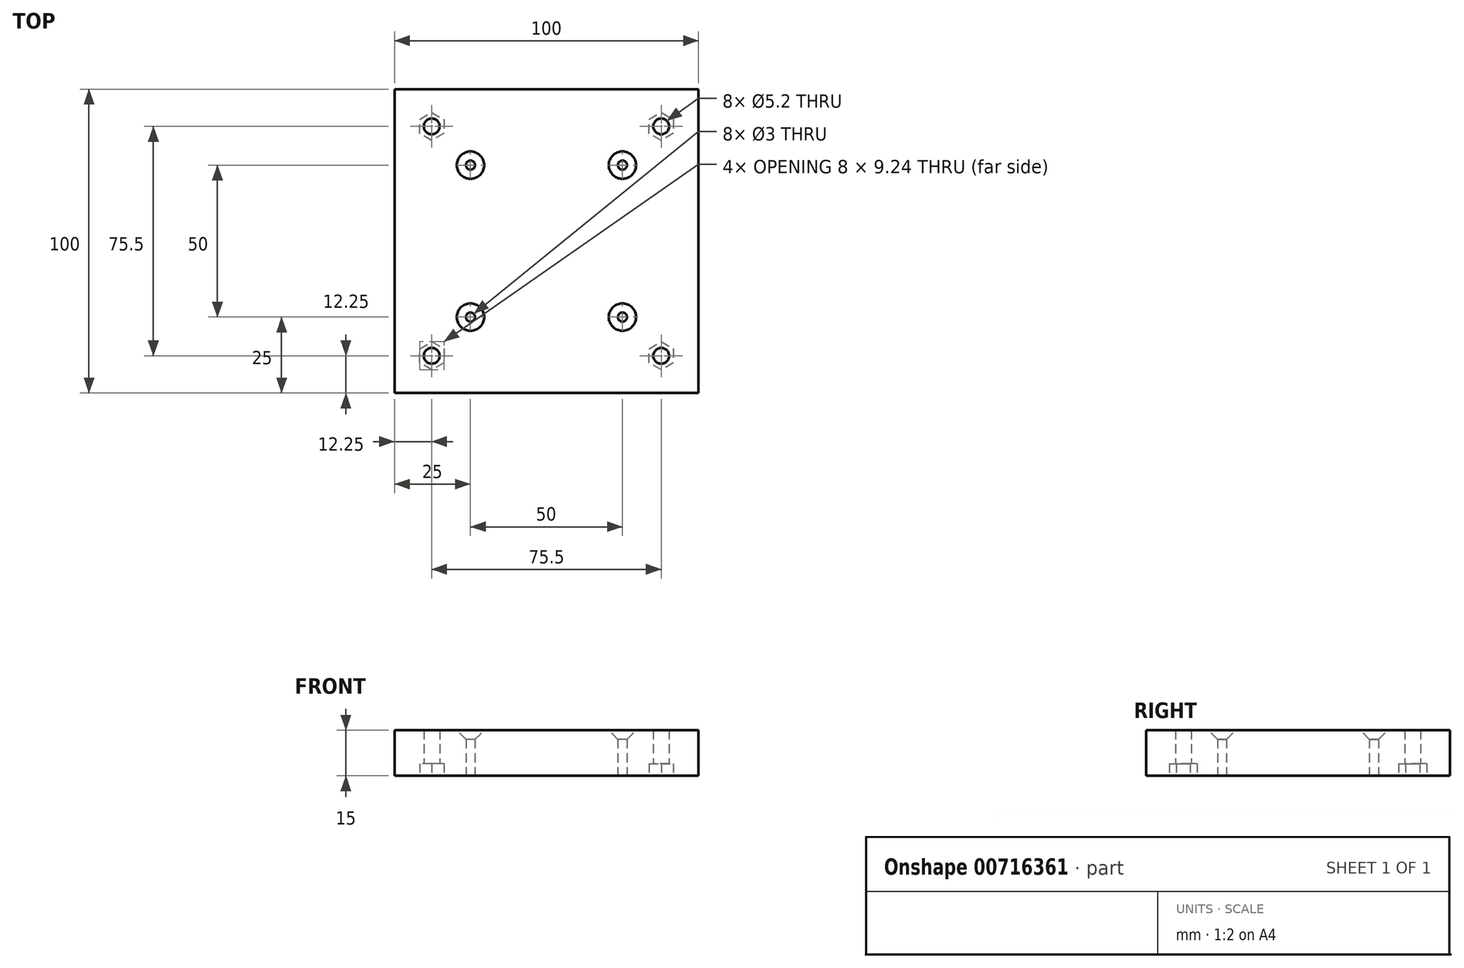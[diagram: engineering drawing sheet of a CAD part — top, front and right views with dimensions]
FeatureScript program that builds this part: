
annotation { "Feature Type Name" : "Feature", "Feature Type Description" : "" }
export const myFeature = defineFeature(function(context is Context, id is Id, definition is map)
    precondition{}
    {
        {
            var Q0;
            Q0=qCreatedBy(makeId("Top.planeOp"),FACE);
            var sketch = newSketch(context, id + "F0", { "sketchPlane" : qUnion([Q0])});
            skLineSegment(sketch, "E0.bottom", {"start": v(-50, 50) * mm, "end": v(50, 50) * mm});
            skLineSegment(sketch, "E0.top", {"start": v(-50, -50) * mm, "end": v(50, -50) * mm});
            skLineSegment(sketch, "E0.left", {"start": v(-50, 50) * mm, "end": v(-50, -50) * mm});
            skLineSegment(sketch, "E0.right", {"start": v(50, 50) * mm, "end": v(50, -50) * mm});
            skCircle(sketch, "E1", {"center": v(-37.75, 37.75) * mm, "radius": 2.6 * mm});
            skCircle(sketch, "E2", {"center": v(-37.75, -37.75) * mm, "radius": 2.6 * mm});
            skCircle(sketch, "E3", {"center": v(37.75, 37.75) * mm, "radius": 2.6 * mm});
            skCircle(sketch, "E4", {"center": v(37.75, -37.75) * mm, "radius": 2.6 * mm});
            skCircle(sketch, "E5.cCircle", {"center": v(-37.75, 37.75) * mm, "radius": 4 * mm, "construction": true});
            skLineSegment(sketch, "E5.0", {"start": v(-41.75, 35.44) * mm, "end": v(-41.75, 40.06) * mm});
            skLineSegment(sketch, "E5.1", {"start": v(-41.75, 40.06) * mm, "end": v(-37.75, 42.37) * mm});
            skLineSegment(sketch, "E5.2", {"start": v(-37.75, 42.37) * mm, "end": v(-33.75, 40.06) * mm});
            skLineSegment(sketch, "E5.3", {"start": v(-33.75, 40.06) * mm, "end": v(-33.75, 35.44) * mm});
            skLineSegment(sketch, "E5.4", {"start": v(-33.75, 35.44) * mm, "end": v(-37.75, 33.13) * mm});
            skLineSegment(sketch, "E5.5", {"start": v(-37.75, 33.13) * mm, "end": v(-41.75, 35.44) * mm});
            skPoint(sketch, "E5.0.midPoint", {"position": v(-41.75, 37.75) * mm});
            skLineSegment(sketch, "E6.0.1.0", {"start": v(-33.75, -35.44) * mm, "end": v(-33.75, -40.06) * mm});
            skLineSegment(sketch, "E6.0.1.1", {"start": v(-37.75, -33.13) * mm, "end": v(-33.75, -35.44) * mm});
            skLineSegment(sketch, "E6.0.1.2", {"start": v(-41.75, -35.44) * mm, "end": v(-37.75, -33.13) * mm});
            skLineSegment(sketch, "E6.0.1.3", {"start": v(-41.75, -40.06) * mm, "end": v(-41.75, -35.44) * mm});
            skLineSegment(sketch, "E6.0.1.4", {"start": v(-37.75, -42.37) * mm, "end": v(-41.75, -40.06) * mm});
            skLineSegment(sketch, "E6.0.1.5", {"start": v(-33.75, -40.06) * mm, "end": v(-37.75, -42.37) * mm});
            skLineSegment(sketch, "E6.1.0.0", {"start": v(41.75, 40.06) * mm, "end": v(41.75, 35.44) * mm});
            skLineSegment(sketch, "E6.1.0.1", {"start": v(37.75, 42.37) * mm, "end": v(41.75, 40.06) * mm});
            skLineSegment(sketch, "E6.1.0.2", {"start": v(33.75, 40.06) * mm, "end": v(37.75, 42.37) * mm});
            skLineSegment(sketch, "E6.1.0.3", {"start": v(33.75, 35.44) * mm, "end": v(33.75, 40.06) * mm});
            skLineSegment(sketch, "E6.1.0.4", {"start": v(37.75, 33.13) * mm, "end": v(33.75, 35.44) * mm});
            skLineSegment(sketch, "E6.1.0.5", {"start": v(41.75, 35.44) * mm, "end": v(37.75, 33.13) * mm});
            skLineSegment(sketch, "E6.1.1.0", {"start": v(41.75, -35.44) * mm, "end": v(41.75, -40.06) * mm});
            skLineSegment(sketch, "E6.1.1.1", {"start": v(37.75, -33.13) * mm, "end": v(41.75, -35.44) * mm});
            skLineSegment(sketch, "E6.1.1.2", {"start": v(33.75, -35.44) * mm, "end": v(37.75, -33.13) * mm});
            skLineSegment(sketch, "E6.1.1.3", {"start": v(33.75, -40.06) * mm, "end": v(33.75, -35.44) * mm});
            skLineSegment(sketch, "E6.1.1.4", {"start": v(37.75, -42.37) * mm, "end": v(33.75, -40.06) * mm});
            skLineSegment(sketch, "E6.1.1.5", {"start": v(41.75, -40.06) * mm, "end": v(37.75, -42.37) * mm});
            skLineSegment(sketch, "E6.direction1", {"start": v(-33.75, 35.44) * mm, "end": v(41.75, 35.44) * mm, "construction": true});
            skLineSegment(sketch, "E6.direction2", {"start": v(-33.75, 35.44) * mm, "end": v(-33.75, -40.06) * mm, "construction": true});
            skCircle(sketch, "E7", {"center": v(-25, 25) * mm, "radius": 1.5 * mm});
            skCircle(sketch, "E8", {"center": v(25, 25) * mm, "radius": 1.5 * mm});
            skCircle(sketch, "E9", {"center": v(25, -25) * mm, "radius": 1.5 * mm});
            skCircle(sketch, "E10", {"center": v(-25, -25) * mm, "radius": 1.5 * mm});
            skSolve(sketch);
        }
        {
            var Q0;
            Q0=makeQuery(id+"F0.imprint","IMPRINT",FACE,{"disambiguationData":[TD([[makeQuery(id+"F0.imprint","IMPRINT",EDGE,{"derivedFrom":sQuery(id+"F0.wireOp",EDGE,"E0.bottom")}),-1.0]])]});
            var Q1;
            Q1=makeQuery(id+"F0.imprint","IMPRINT",FACE,{"disambiguationData":[TD([[makeQuery(id+"F0.imprint","IMPRINT",EDGE,{"derivedFrom":sQuery(id+"F0.wireOp",EDGE,"E3")}),-1.0]])]});
            var Q2;
            Q2=makeQuery(id+"F0.imprint","IMPRINT",FACE,{"disambiguationData":[TD([[makeQuery(id+"F0.imprint","IMPRINT",EDGE,{"derivedFrom":sQuery(id+"F0.wireOp",EDGE,"E1")}),-1.0]])]});
            var Q3;
            Q3=makeQuery(id+"F0.imprint","IMPRINT",FACE,{"disambiguationData":[TD([[makeQuery(id+"F0.imprint","IMPRINT",EDGE,{"derivedFrom":sQuery(id+"F0.wireOp",EDGE,"E2")}),-1.0]])]});
            var Q4;
            Q4=makeQuery(id+"F0.imprint","IMPRINT",FACE,{"disambiguationData":[TD([[makeQuery(id+"F0.imprint","IMPRINT",EDGE,{"derivedFrom":sQuery(id+"F0.wireOp",EDGE,"E4")}),-1.0]])]});
            extrude(context, id + "F1", {"entities" : qUnion([Q0, Q1, Q2, Q3, Q4]), "depth" : 15 * mm, "offsetDistance" : 25 * mm});
        }
        {
            var Q0;
            Q0=makeQuery(id+"F0.imprint","IMPRINT",FACE,{"disambiguationData":[TD([[makeQuery(id+"F0.imprint","IMPRINT",EDGE,{"derivedFrom":sQuery(id+"F0.wireOp",EDGE,"E1")}),-1.0]])]});
            var Q1;
            Q1=makeQuery(id+"F0.imprint","IMPRINT",FACE,{"disambiguationData":[TD([[makeQuery(id+"F0.imprint","IMPRINT",EDGE,{"derivedFrom":sQuery(id+"F0.wireOp",EDGE,"E3")}),-1.0]])]});
            var Q2;
            Q2=makeQuery(id+"F0.imprint","IMPRINT",FACE,{"disambiguationData":[TD([[makeQuery(id+"F0.imprint","IMPRINT",EDGE,{"derivedFrom":sQuery(id+"F0.wireOp",EDGE,"E4")}),-1.0]])]});
            var Q3;
            Q3=makeQuery(id+"F0.imprint","IMPRINT",FACE,{"disambiguationData":[TD([[makeQuery(id+"F0.imprint","IMPRINT",EDGE,{"derivedFrom":sQuery(id+"F0.wireOp",EDGE,"E2")}),-1.0]])]});
            extrude(context, id + "F2", {"entities" : qUnion([Q0, Q1, Q2, Q3]), "operationType" : NewBodyOperationType.REMOVE, "depth" : 4 * mm, "offsetDistance" : 25 * mm});
        }
        {
            var Q0;
            Q0=makeQuery(id+"F1.opExtrude","CAP_EDGE",EDGE,{"disambiguationData":[OSD([sQuery(id+"F0.wireOp",EDGE,"E7")])],"isStart":false});
            var Q1;
            Q1=makeQuery(id+"F1.opExtrude","CAP_EDGE",EDGE,{"disambiguationData":[OSD([sQuery(id+"F0.wireOp",EDGE,"E8")])],"isStart":false});
            var Q2;
            Q2=makeQuery(id+"F1.opExtrude","CAP_EDGE",EDGE,{"disambiguationData":[OSD([sQuery(id+"F0.wireOp",EDGE,"E9")])],"isStart":false});
            var Q3;
            Q3=makeQuery(id+"F1.opExtrude","CAP_EDGE",EDGE,{"disambiguationData":[OSD([sQuery(id+"F0.wireOp",EDGE,"E10")])],"isStart":false});
            chamfer(context, id + "F3", {"entities" : qUnion([Q0, Q1, Q2, Q3]), "width" : 3 * mm, "tangentPropagation" : true});
        }
    });
